# Revit family: Faucet-Two_Handle-American_Standard-Studio_S-7105.8X1_Series
name_source: partatom
category: Plumbing Fixtures
revit_build: Autodesk Revit 2014 (Build: 20130308_1515(x64)
units: mm (PartAtom-declared; Revit-internal decimal feet)

## types (2) — shared parameters
ADA Compliant = Yes
Assembly Code = D2020300
CW Connection = Yes
CWFU = 1.5
Cold Water Connection Diameter = 1/2"
Cold Water Connection Radius = 1/4"
Default Elevation = 0"
Finish = Brass-American Standard-002-Polished Chrome
Flow Rate = 1.2 gpm/ 4.5 L/min.
HW Connection = No
HWFU = 1.5
Height = 8 11/16"
Hot Water Connection Diameter = 1"
Hot Water Connection Radius = 1/4"
Installation Type = Deck Mounted
Length = 8"
Manufacturer = American Standard
Material = Brass-American Standard-002-Polished Chrome
Price = Prices may vary. Please consult Manufacturer Representative for most up-to-date price list.
Product Documentation Link = https://www.americanstandard-us.com
Product Page URL = https://www.americanstandard-us.com
Specification = Two-handle widespread lavatory faucet shall feature cast brass valve bodies with flexible hose connections for 6" to 12" installations. Shall also feature 1/4 turn washerless ceramic disc valve cartridges. Shall also feature a metal drain body with stainless steel cable actuation.
URL = https://www.americanstandard-us.com
Vent Connection = Yes
WFU = 2
Warranty Information = Limited Lifetime Function and Finish Warranty
Waste Connection = Yes
Width = 4 7/8"

## per-type parameters (varying)
| type | Description | Knob Handles | Lever Handles |
| 7105801 | Studio S Two-Handle Widespread Lavatory Faucet. Metal Speed Connect® pop-up drain. Metal lever handles. | No | Yes |
| 7105821 | Studio S Two-Handle Widespread Lavatory Faucet. Metal Speed Connect® pop-up drain. Metal knob handles. | Yes | No |

note: column(s) folded — value = type name in every type: Model

## geometry (parser evidence)
native form markers: Sweep x1
no freeform markers — native parametric forms only
